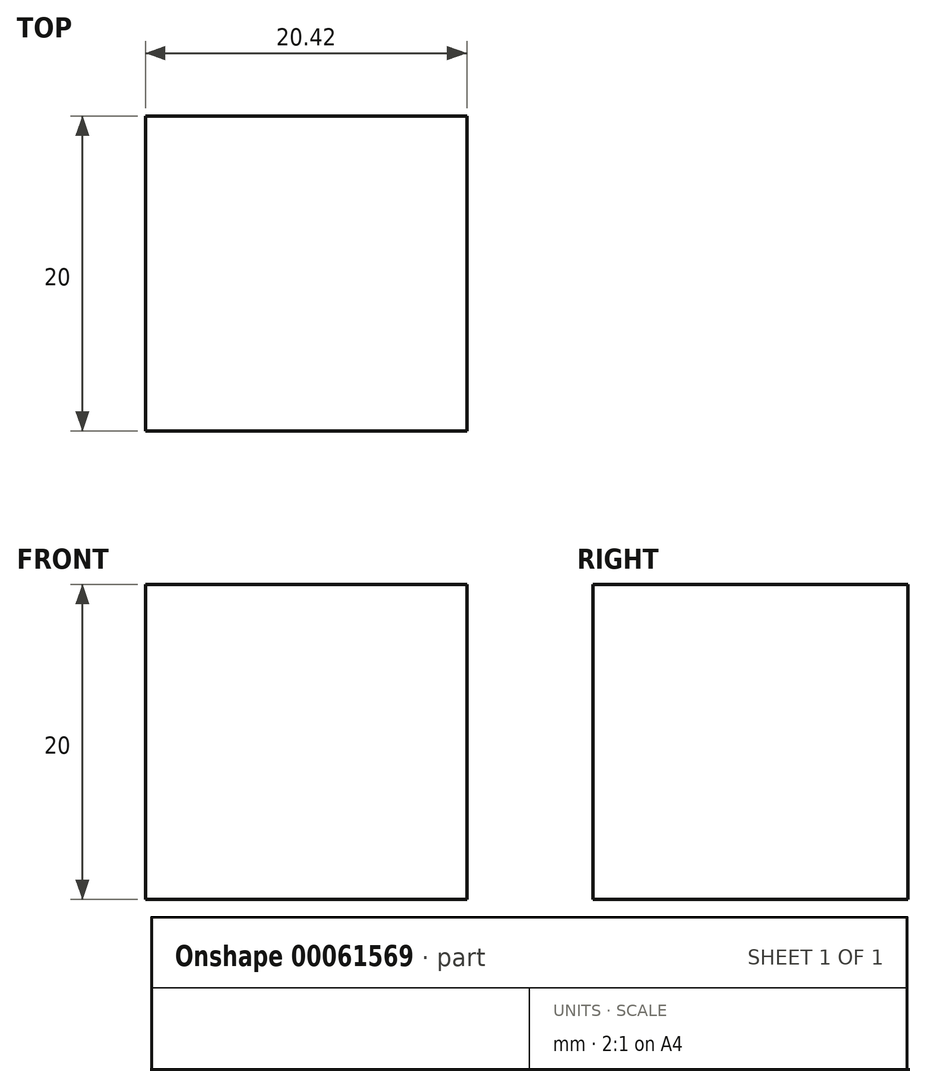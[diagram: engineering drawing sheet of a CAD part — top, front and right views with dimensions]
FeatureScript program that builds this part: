
annotation { "Feature Type Name" : "Feature", "Feature Type Description" : "" }
export const myFeature = defineFeature(function(context is Context, id is Id, definition is map)
    precondition{}
    {
        {
            var Q0;
            Q0=qCreatedBy(makeId("Front.planeOp"),FACE);
            var sketch = newSketch(context, id + "F1", { "sketchPlane" : qUnion([Q0])});
            skLineSegment(sketch, "E0.rect.bottom", {"start": v(10.21, 10) * mm, "end": v(-10.21, 10) * mm});
            skLineSegment(sketch, "E0.rect.top", {"start": v(10.21, -10) * mm, "end": v(-10.21, -10) * mm});
            skLineSegment(sketch, "E0.rect.left", {"start": v(10.21, 10) * mm, "end": v(10.21, -10) * mm});
            skLineSegment(sketch, "E0.rect.right", {"start": v(-10.21, 10) * mm, "end": v(-10.21, -10) * mm});
            skPoint(sketch, "E0.rect.middle", {"position": v(0, 0) * mm});
            skSolve(sketch);
        }
        {
            var Q0;
            Q0=makeQuery(id+"F1.imprint","IMPRINT",FACE,{"disambiguationData":[TD([[makeQuery(id+"F1.imprint","IMPRINT",EDGE,{"derivedFrom":sQuery(id+"F1.wireOp",EDGE,"E0.rect.bottom")}),1.0]])]});
            extrude(context, id + "F0", {"entities" : qUnion([Q0]), "depth" : 20 * mm});
        }
    });
